# Revit family: EP-3007_RFA
name_source: partatom
category: Aparatos sanitarios
units: mm (PartAtom-declared; Revit-internal decimal feet)

## family parameters
Activar corte en vistas = No
Compartido = No
Corte con vacíos al cargar = No
Cota de conector redondo = Usar diámetro
Mantener orientación de anotación = No
Número OmniClass = 23.45.00.00
Punto de cálculo de habitación = No
Se basa en plano de trabajo = No
Siempre vertical = Sí
Tipo de pieza = Normal
Título OmniClass = Sanitary, Laundry, and Cleaning Equipment

## types (1)
- EP-3007
    Accesorios = Placa para empotrar en tablaroca. Llave para la tuerca del cartucho. Llave para aireador.
    Chrome = Brass Chromed
    Comentarios de tipo = Ensambles Básicos para Lavabo
    Conexión AC = Sí
    Conexión AF = Sí
    Descripción = Monomando a pared incluye contra de push.
    Elevación por defecto = 45"
    Fabricante = Helvex
    Imagen de tipo = EP-3007.png
    Inlet Threads = ½" - 14 NPSM
    Material = Latón
    Max. Working Pressure = 85.3 psi
    Min. Working Pressure = 14.2 psi
    Modelo = EP-3007
    Operación = Para abrir el flujo de agua, levante la palanca y
para cerrar empuje la palanca. Para ajustar la
temperatura del agua, gire a la izquierda para
caliente y gire a la derecha para fría.
    URL = https://helvex.com.mx

## geometry (parser evidence)
native form markers: Sweep x2
no freeform markers — native parametric forms only
